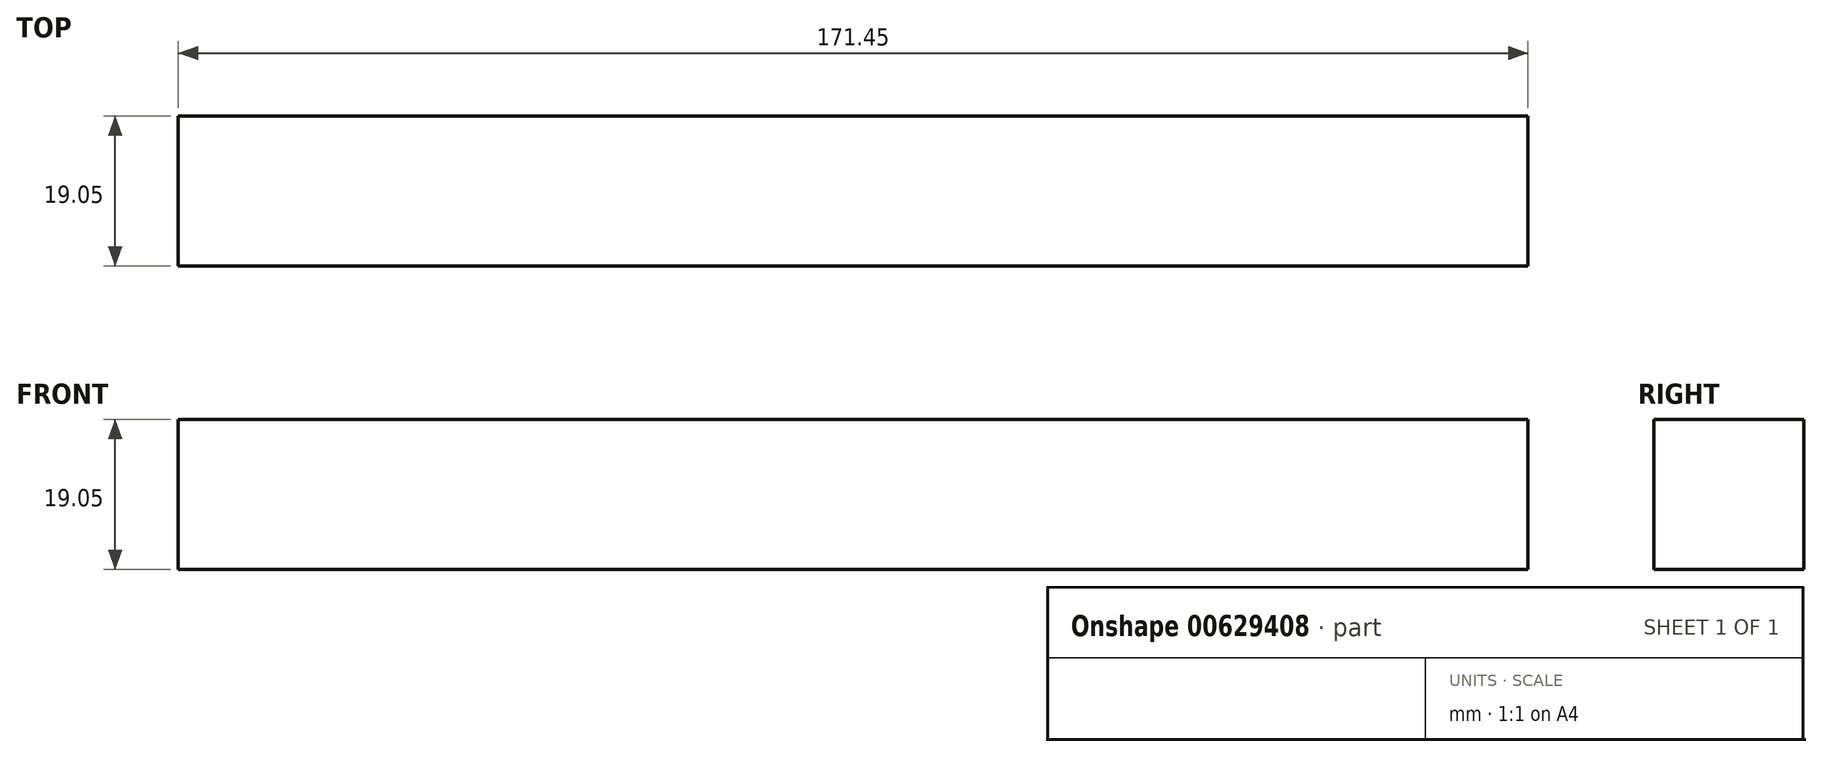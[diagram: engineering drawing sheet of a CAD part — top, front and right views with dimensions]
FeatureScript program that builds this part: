
annotation { "Feature Type Name" : "Feature", "Feature Type Description" : "" }
export const myFeature = defineFeature(function(context is Context, id is Id, definition is map)
    precondition{}
    {
        {
            var Q0;
            Q0=qCreatedBy(makeId("Front.planeOp"),FACE);
            var sketch = newSketch(context, id + "F0", { "sketchPlane" : qUnion([Q0])});
            skLineSegment(sketch, "E0.bottom", {"start": v(0, 0) * mm, "end": v(171.45, 0) * mm});
            skLineSegment(sketch, "E0.top", {"start": v(0, 19.05) * mm, "end": v(171.45, 19.05) * mm});
            skLineSegment(sketch, "E0.left", {"start": v(0, 0) * mm, "end": v(0, 19.05) * mm});
            skLineSegment(sketch, "E0.right", {"start": v(171.45, 0) * mm, "end": v(171.45, 19.05) * mm});
            skSolve(sketch);
        }
        {
            var Q0;
            Q0=qSketchRegion(id+"F0",true);
            extrude(context, id + "F1", {"entities" : qUnion([Q0]), "depth" : 19.05 * mm, "offsetDistance" : 25.4 * mm});
        }
    });
